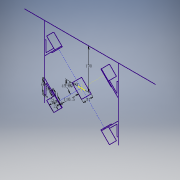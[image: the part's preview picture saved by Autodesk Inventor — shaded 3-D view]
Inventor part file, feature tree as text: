
AUTODESK INVENTOR PART (.ipt)
format: ipt  version: 2016 (Build 200138000, 138)  size: 121,856 bytes
history: native  units: mm
features: sketch x1
ambient origin geometry x8: Origin, YZ Plane, XZ Plane, XY Plane, X Axis, Y Axis, Z Axis, Center Point
feature tree (1):
  sketch  "草图1"  dims[d0=45.0deg d1=57.0mm d2=110.5mm d3=45.0deg d4=21.0mm d5=21.0mm d6=48.0mm d7=3.0mm d8=41.0mm d25=60.0mm d26=60.0mm d27=6.0mm d28=6.0mm d29=170.0mm]
